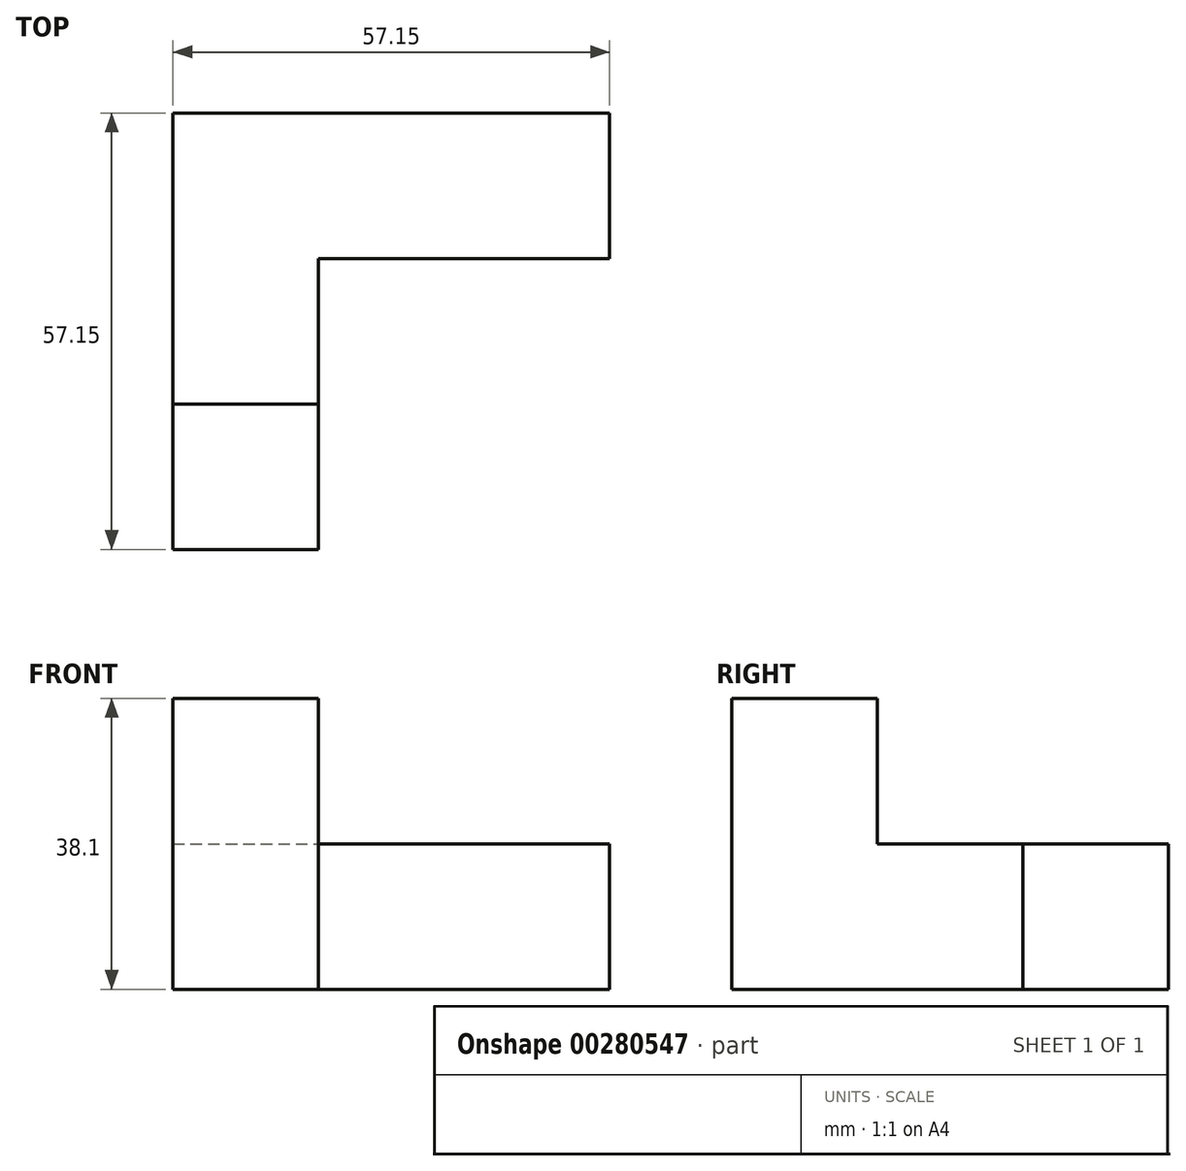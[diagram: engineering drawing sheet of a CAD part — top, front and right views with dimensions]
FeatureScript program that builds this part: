
annotation { "Feature Type Name" : "Feature", "Feature Type Description" : "" }
export const myFeature = defineFeature(function(context is Context, id is Id, definition is map)
    precondition{}
    {
        {
            var Q0;
            Q0=qCreatedBy(makeId("Top.planeOp"),FACE);
            var sketch = newSketch(context, id + "F0", { "sketchPlane" : qUnion([Q0])});
            skLineSegment(sketch, "E0.bottom", {"start": v(0, 0) * mm, "end": v(19.05, 0) * mm});
            skLineSegment(sketch, "E0.top", {"start": v(0, 57.15) * mm, "end": v(57.15, 57.15) * mm});
            skLineSegment(sketch, "E0.left", {"start": v(0, 0) * mm, "end": v(0, 57.15) * mm});
            skLineSegment(sketch, "E0.right", {"start": v(57.15, 38.1) * mm, "end": v(57.15, 57.15) * mm});
            skLineSegment(sketch, "E1", {"start": v(57.15, 57.15) * mm, "end": v(57.15, 38.1) * mm});
            skLineSegment(sketch, "E2", {"start": v(57.15, 38.1) * mm, "end": v(19.05, 38.1) * mm});
            skLineSegment(sketch, "E3", {"start": v(19.05, 38.1) * mm, "end": v(19.05, 0) * mm});
            skSolve(sketch);
        }
        {
            var Q0;
            Q0 = qSketchRegion(id + "F0", true);
            extrude(context, id + "F1", {"entities" : qUnion([Q0]), "depth" : 19.05 * mm});
        }
        {
            var Q0;
            Q0=makeQuery(id+"F1.opExtrude","CAP_FACE",FACE,{"disambiguationData":[OSD([sQuery(id+"F0.wireOp",EDGE,"E0.bottom"),sQuery(id+"F0.wireOp",EDGE,"E0.top"),sQuery(id+"F0.wireOp",EDGE,"E0.left"),sQuery(id+"F0.wireOp",EDGE,"E1"),sQuery(id+"F0.wireOp",EDGE,"E2"),sQuery(id+"F0.wireOp",EDGE,"E3")])],"isStart":false});
            var sketch = newSketch(context, id + "F2", { "sketchPlane" : qUnion([Q0])});
            skLineSegment(sketch, "E4.bottom", {"start": v(0, 0) * mm, "end": v(19.05, 0) * mm});
            skLineSegment(sketch, "E4.top", {"start": v(0, 19.05) * mm, "end": v(19.05, 19.05) * mm});
            skLineSegment(sketch, "E4.left", {"start": v(0, 0) * mm, "end": v(0, 19.05) * mm});
            skLineSegment(sketch, "E4.right", {"start": v(19.05, 0) * mm, "end": v(19.05, 19.05) * mm});
            skSolve(sketch);
        }
        {
            var Q0;
            Q0 = qSketchRegion(id + "F2", true);
            extrude(context, id + "F3", {"entities" : qUnion([Q0]), "operationType" : NewBodyOperationType.ADD, "depth" : 19.05 * mm});
        }
    });
